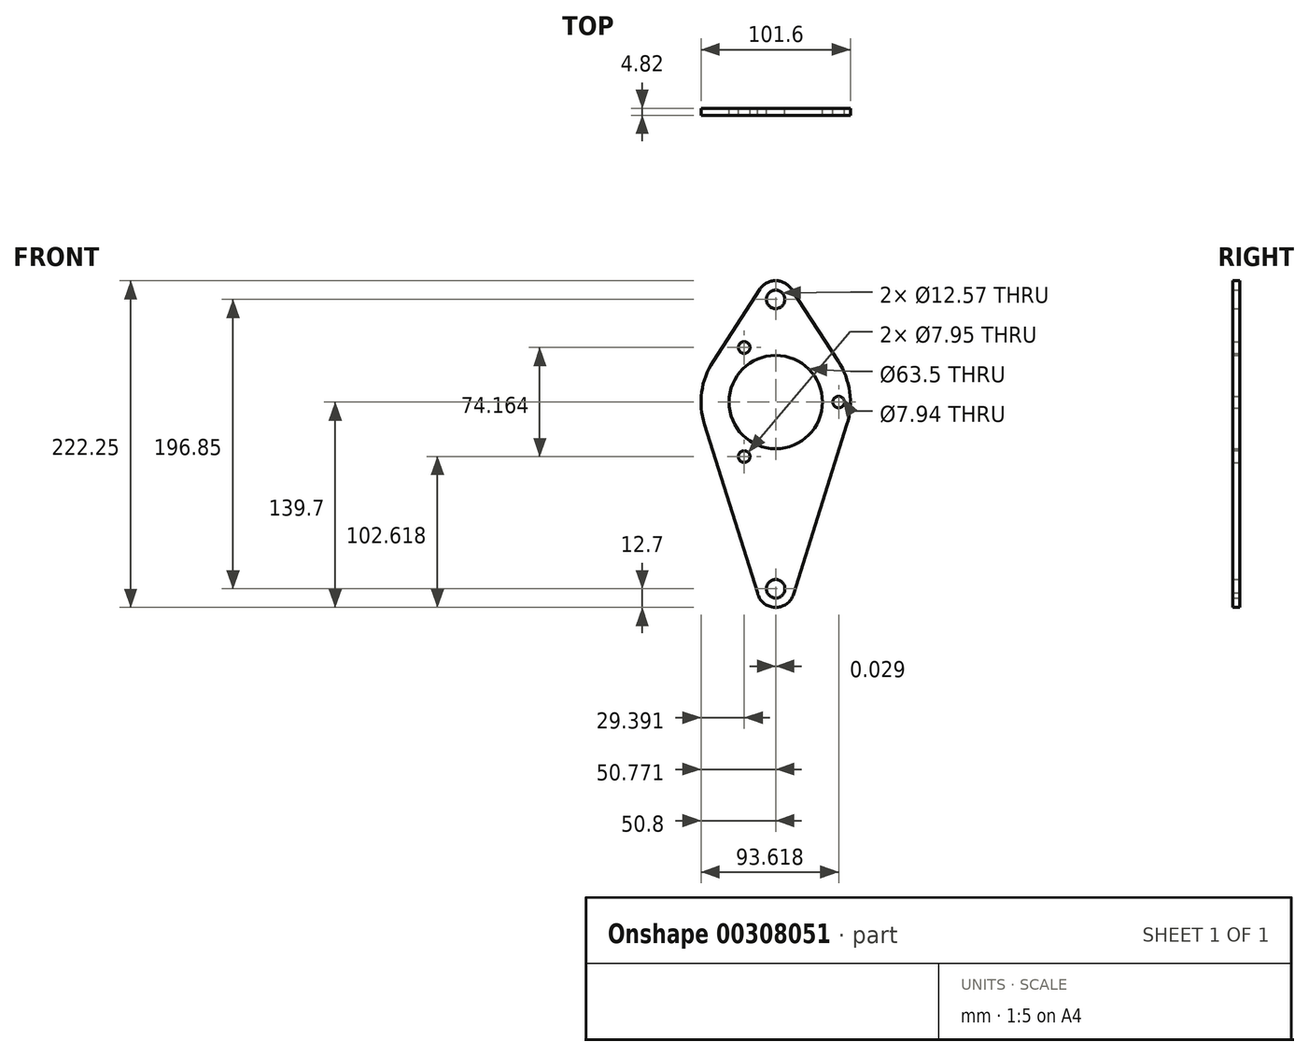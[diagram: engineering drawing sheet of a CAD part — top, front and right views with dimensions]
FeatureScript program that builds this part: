
annotation { "Feature Type Name" : "Feature", "Feature Type Description" : "" }
export const myFeature = defineFeature(function(context is Context, id is Id, definition is map)
    precondition{}
    {
        {
            var Q0;
            Q0=qCreatedBy(makeId("Front.planeOp"),FACE);
            var sketch = newSketch(context, id + "F0", { "sketchPlane" : qUnion([Q0])});
            skArc(sketch, "E0", {"start": v(10.61, 76.78) * mm, "mid": v(-0.03, 82.55) * mm, "end": v(-10.68, 76.77) * mm});
            skArc(sketch, "E1", {"start": v(-12.4, -129.73) * mm, "mid": v(-0.56, -139.69) * mm, "end": v(12.12, -130.8) * mm});
            skLineSegment(sketch, "E2", {"start": v(-12.4, -129.73) * mm, "end": v(-48.45, -15.26) * mm});
            skLineSegment(sketch, "E3", {"start": v(12.12, -130.8) * mm, "end": v(48.46, -15.24) * mm});
            skLineSegment(sketch, "E4", {"start": v(-42.59, 27.7) * mm, "end": v(-10.68, 76.77) * mm});
            skLineSegment(sketch, "E5", {"start": v(42.57, 27.73) * mm, "end": v(10.61, 76.78) * mm});
            skCircle(sketch, "E6", {"center": v(-0.03, 69.85) * mm, "radius": 6.29 * mm});
            skCircle(sketch, "E7", {"center": v(0, -127) * mm, "radius": 6.29 * mm});
            skArc(sketch, "E8", {"start": v(42.85, 3.97) * mm, "mid": v(42.74, 3.97) * mm, "end": v(42.63, 3.96) * mm});
            skCircle(sketch, "E9", {"center": v(-21.4, 37.08) * mm, "radius": 3.98 * mm});
            skCircle(sketch, "E10.MirrorC", {"center": v(-21.4, -37.08) * mm, "radius": 3.98 * mm});
            skArc(sketch, "E11", {"start": v(48.46, -15.24) * mm, "mid": v(50.33, 6.9) * mm, "end": v(42.57, 27.73) * mm});
            skArc(sketch, "E12.trimOffspring", {"start": v(-42.59, 27.7) * mm, "mid": v(-50.33, 6.87) * mm, "end": v(-48.45, -15.26) * mm});
            skCircle(sketch, "E13", {"center": v(0, 0) * mm, "radius": 31.75 * mm});
            skCircle(sketch, "E14", {"center": v(42.82, 0) * mm, "radius": 3.97 * mm});
            skArc(sketch, "E15.trimOffspring", {"start": v(42.63, -3.96) * mm, "mid": v(42.74, -3.97) * mm, "end": v(42.85, -3.97) * mm});
            skSolve(sketch);
        }
        {
            var Q0;
            Q0=qSketchRegion(id+"F0",true);
            extrude(context, id + "F1", {"entities" : qUnion([Q0]), "endBound" : BoundingType.SYMMETRIC, "depth" : 4.83 * mm, "offsetDistance" : 25.4 * mm});
        }
    });
